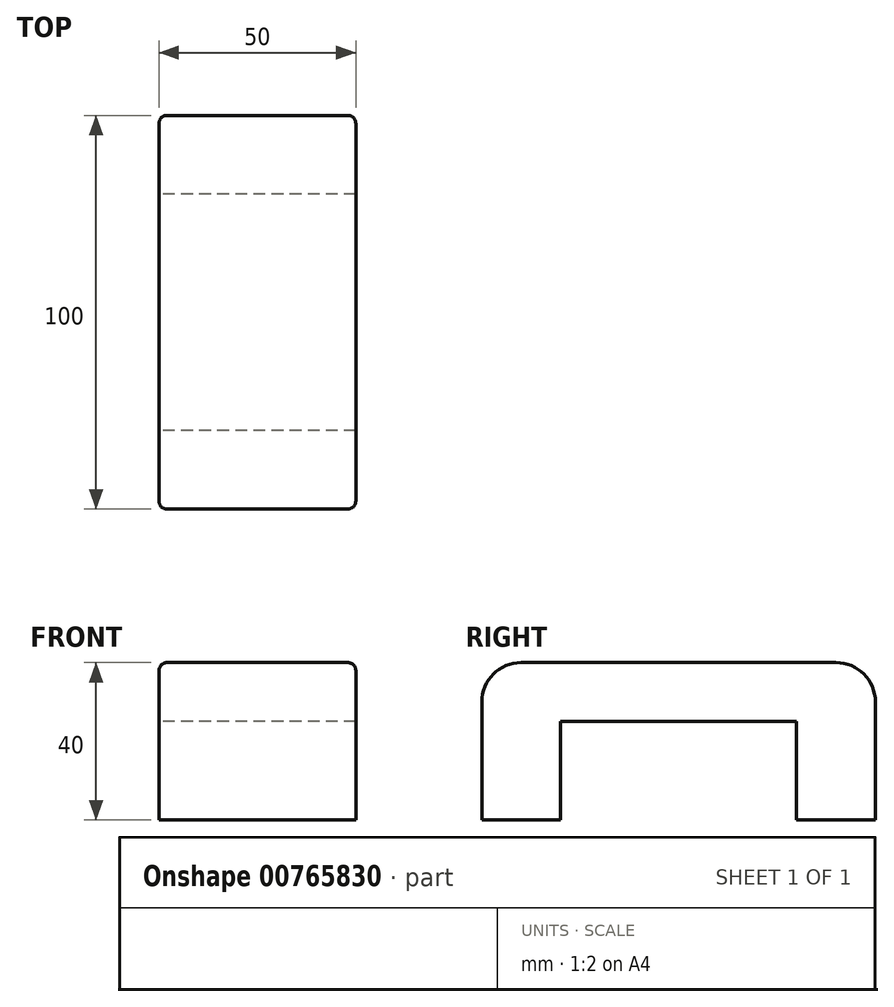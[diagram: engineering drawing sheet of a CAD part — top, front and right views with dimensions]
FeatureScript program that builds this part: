
annotation { "Feature Type Name" : "Feature", "Feature Type Description" : "" }
export const myFeature = defineFeature(function(context is Context, id is Id, definition is map)
    precondition{}
    {
        {
            var Q0;
            Q0=qCreatedBy(makeId("Right.planeOp"),FACE);
            var sketch = newSketch(context, id + "F0", { "sketchPlane" : qUnion([Q0])});
            skLineSegment(sketch, "E0", {"start": v(-34.3, 15) * mm, "end": v(65.7, 15) * mm});
            skLineSegment(sketch, "E1", {"start": v(-34.3, 15) * mm, "end": v(-34.3, 0) * mm});
            skLineSegment(sketch, "E2", {"start": v(65.7, 15) * mm, "end": v(65.7, 0) * mm});
            skLineSegment(sketch, "E3", {"start": v(65.7, 0) * mm, "end": v(-34.3, 0) * mm});
            skLineSegment(sketch, "E4", {"start": v(65.7, 0) * mm, "end": v(65.7, -25) * mm});
            skLineSegment(sketch, "E5", {"start": v(65.7, -25) * mm, "end": v(45.7, -25) * mm});
            skLineSegment(sketch, "E6", {"start": v(45.7, -25) * mm, "end": v(45.7, 0) * mm});
            skLineSegment(sketch, "E7", {"start": v(-34.3, 0) * mm, "end": v(-34.3, -25) * mm});
            skLineSegment(sketch, "E8", {"start": v(-34.3, -25) * mm, "end": v(-14.3, -25) * mm});
            skLineSegment(sketch, "E9", {"start": v(-14.3, -25) * mm, "end": v(-14.3, 0) * mm});
            skSolve(sketch);
        }
        {
            var Q0;
            Q0 = qSketchRegion(id + "F0", true);
            extrude(context, id + "F1", {"entities" : qUnion([Q0]), "depth" : 50 * mm, "offsetDistance" : 25 * mm});
        }
        {
            var Q0;
            Q0=makeQuery(id+"F1.opExtrude","SWEPT_EDGE",EDGE,{"disambiguationData":[OSD([sQuery(id+"F0.wireOp",EDGE,"E0"),sQuery(id+"F0.wireOp",EDGE,"E1")])]});
            var Q1;
            Q1=makeQuery(id+"F1.opExtrude","SWEPT_EDGE",EDGE,{"disambiguationData":[OSD([sQuery(id+"F0.wireOp",EDGE,"E0"),sQuery(id+"F0.wireOp",EDGE,"E2")])]});
            fillet(context, id + "F2", {"entities" : qUnion([Q0, Q1]), "radius" : 10 * mm, "tangentPropagation" : true, "allowEdgeOverflow" : false});
        }
        {
            var Q0;
            Q0=makeQuery(id+"F1.opExtrude","CAP_EDGE",EDGE,{"disambiguationData":[OSD([sQuery(id+"F0.wireOp",EDGE,"E0")])],"isStart":false});
            var Q1;
            Q1=makeQuery(id+"F1.opExtrude","CAP_EDGE",EDGE,{"disambiguationData":[OSD([sQuery(id+"F0.wireOp",EDGE,"E0")])],"isStart":true});
            fillet(context, id + "F3", {"entities" : qUnion([Q0, Q1]), "radius" : 2 * mm, "tangentPropagation" : true, "allowEdgeOverflow" : false});
        }
    });
